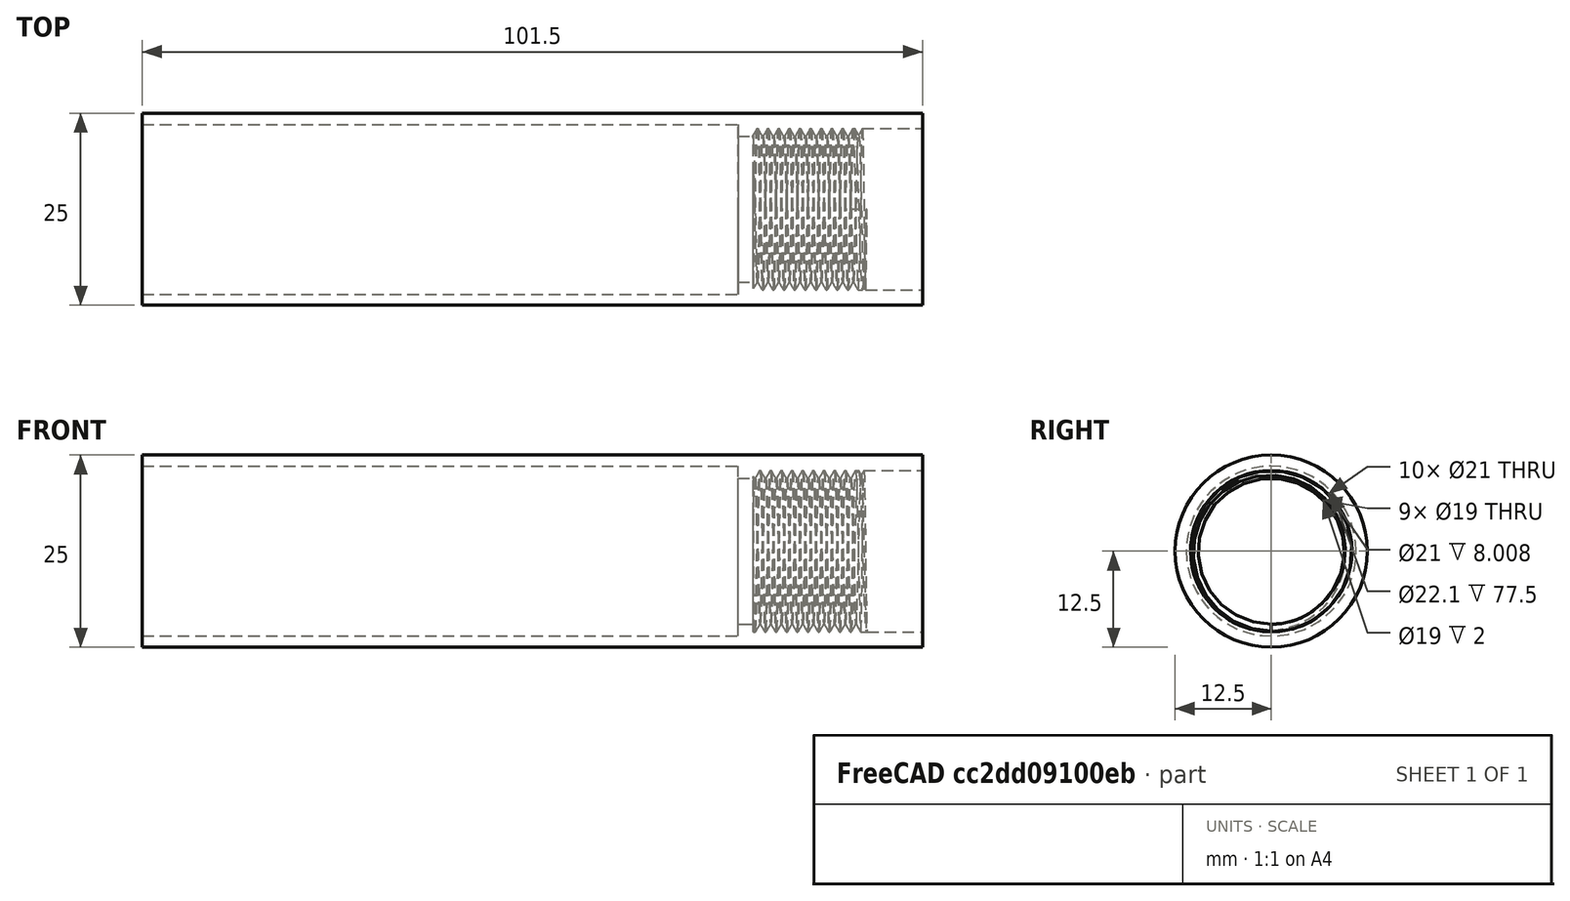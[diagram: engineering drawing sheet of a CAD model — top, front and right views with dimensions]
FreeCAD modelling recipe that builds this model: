
FCSTD DOCUMENT  (FreeCAD 0.17R13541 (Git))
Label: ERG-T-01-BH
License: All rights reserved
LicenseURL: http://en.wikipedia.org/wiki/All_rights_reserved
objects: Drawing::FeatureViewPython×39, Part::Cylinder×6, Part::Cut×5, Drawing::FeatureViewPart×4, Part::MultiFuse×3, Drawing::FeaturePage×2, Sketcher::SketchObject×2, Part::Helix×2, Part::Sweep×2, Part::Feature×1
note: 21 computed .brp shape members not serialized (recipe doc carries the construction recipe); baked Part::Feature solids carry a one-line shape summary decoded from their .brp

FEATURE [Drawing::FeatureViewPython] dim130  # drawing view (typed FeaturePython)
  Rotation = 0
  ViewResult = <g> \n  <line x1="95.000000" y1="103.600000" x2="95.000000" y2="144.306302" style="stroke:rgb(255,0,0);stroke-width:0.10" />\n<line x1="47.000000" y1="102.500000" x2="47.000000" y2="144.306302" style="stroke:rgb(255,0,0);stroke-width:0.10" />\n<line x1="95.000000" y1="143.306302" x2="47.000000" y2="143.306302" style="stroke:rgb(255,0,0);stroke-width:0.10" /> \n  <polygon points="47.000000,143.306302 49.000000,143.806302 49.500000,143.306302 49.000000,142.806302" style="fill:rgb(255,0,0);stroke:rgb(255,0,0);stroke-width:0" /><polygon points="95.000000,143.306302 93.000000,142.806302 92.500000,143.306302 93.000000,143.806302" style="fill:rgb(255,0,0);stroke:rgb(255,0,0);stroke-width:0" /> \n  <text x="71.000000" y="141.306302" font-family="inherit" font-size="3.6" fill="rgb(0,0,0)" text-anchor="middle" transform="rotate(0.000000 71.000000,141.306302)" >24</text> </g>
  Visible = true
  X = 0
  Y = 0
  arrowL1 = 2
  arrowL2 = 0.5
  arrowW = 1
  arrow_scheme = 0
  autoPlaceOffset = 2
  autoPlaceText = true
  click1_x = 59.2162
  click1_y = 143.306
  click2_x = 59.2162
  click2_y = 143.306
  comma_decimal_place = false
  dimension_line_overshoot = 1
  gap_datum_points = 0
  halfDimension_linear = false
  lineColor = rgb(255,0,0)
  strokeWidth = 0.1
  textFormat_linear = %(value)3.3f
  textRenderer_color = rgb(0,0,0)
  textRenderer_family = inherit
  textRenderer_size = 3.6
  unit_custom_scale = 1.7
  unit_scheme = 0
FEATURE [Drawing::FeatureViewPython] dim131  # drawing view (typed FeaturePython)
  Rotation = 0
  ViewResult = <g> \n  <line x1="95.000000" y1="103.600000" x2="95.000000" y2="144.274206" style="stroke:rgb(255,0,0);stroke-width:0.10" />\n<line x1="250.000000" y1="106.500000" x2="250.000000" y2="144.274206" style="stroke:rgb(255,0,0);stroke-width:0.10" />\n<line x1="95.000000" y1="143.274206" x2="250.000000" y2="143.274206" style="stroke:rgb(255,0,0);stroke-width:0.10" /> \n  <polygon points="250.000000,143.274206 248.000000,142.774206 247.500000,143.274206 248.000000,143.774206" style="fill:rgb(255,0,0);stroke:rgb(255,0,0);stroke-width:0" /><polygon points="95.000000,143.274206 97.000000,143.774206 97.500000,143.274206 97.000000,142.774206" style="fill:rgb(255,0,0);stroke:rgb(255,0,0);stroke-width:0" /> \n  <text x="172.500000" y="141.274206" font-family="inherit" font-size="3.6" fill="rgb(0,0,0)" text-anchor="middle" transform="rotate(0.000000 172.500000,141.274206)" >77.5</text> </g>
  Visible = true
  X = 0
  Y = 0
  arrowL1 = 2
  arrowL2 = 0.5
  arrowW = 1
  arrow_scheme = 0
  autoPlaceOffset = 2
  autoPlaceText = true
  click1_x = 247.264
  click1_y = 143.274
  click2_x = 247.264
  click2_y = 143.274
  comma_decimal_place = false
  dimension_line_overshoot = 1
  gap_datum_points = 0
  halfDimension_linear = false
  lineColor = rgb(255,0,0)
  strokeWidth = 0.1
  textFormat_linear = %(value)3.3f
  textRenderer_color = rgb(0,0,0)
  textRenderer_family = inherit
  textRenderer_size = 3.6
  unit_custom_scale = 1.7
  unit_scheme = 0
FEATURE [Drawing::FeatureViewPython] dim132  # drawing view (typed FeaturePython)
  Rotation = 0
  ViewResult = <g> \n  <line x1="95.000000" y1="100.500000" x2="95.000000" y2="91.946246" style="stroke:rgb(255,0,0);stroke-width:0.10" />\n<line x1="91.000000" y1="100.500000" x2="91.000000" y2="91.946246" style="stroke:rgb(255,0,0);stroke-width:0.10" />\n<line x1="95.000000" y1="92.946246" x2="91.000000" y2="92.946246" style="stroke:rgb(255,0,0);stroke-width:0.10" /> \n  <polygon points="91.000000,92.946246 89.000000,92.446246 88.500000,92.946246 89.000000,93.446246" style="fill:rgb(255,0,0);stroke:rgb(255,0,0);stroke-width:0" /><polygon points="95.000000,92.946246 97.000000,93.446246 97.500000,92.946246 97.000000,92.446246" style="fill:rgb(255,0,0);stroke:rgb(255,0,0);stroke-width:0" /> \n  <text x="93.000000" y="90.946246" font-family="inherit" font-size="3.6" fill="rgb(0,0,0)" text-anchor="middle" transform="rotate(0.000000 93.000000,90.946246)" >2</text> </g>
  Visible = true
  X = 0
  Y = 0
  arrowL1 = 2
  arrowL2 = 0.5
  arrowW = 1
  arrow_scheme = 0
  autoPlaceOffset = 2
  autoPlaceText = true
  click1_x = 91.8628
  click1_y = 92.9462
  click2_x = 91.8628
  click2_y = 92.9462
  comma_decimal_place = false
  dimension_line_overshoot = 1
  gap_datum_points = 0
  halfDimension_linear = false
  lineColor = rgb(255,0,0)
  strokeWidth = 0.1
  textFormat_linear = %(value)3.3f
  textRenderer_color = rgb(0,0,0)
  textRenderer_family = inherit
  textRenderer_size = 3.6
  unit_custom_scale = 1.7
  unit_scheme = 0
FEATURE [Drawing::FeatureViewPython] dim133  # drawing view (typed FeaturePython)
  Rotation = 0
  ViewResult = <g> \n  <line x1="62.208000" y1="60.500000" x2="62.208000" y2="72.297691" style="stroke:rgb(255,0,0);stroke-width:0.10" />\n<line x1="91.000000" y1="62.500000" x2="91.000000" y2="72.297691" style="stroke:rgb(255,0,0);stroke-width:0.10" />\n<line x1="62.208000" y1="71.297691" x2="91.000000" y2="71.297691" style="stroke:rgb(255,0,0);stroke-width:0.10" /> \n  <polygon points="91.000000,71.297691 89.000000,70.797691 88.500000,71.297691 89.000000,71.797691" style="fill:rgb(255,0,0);stroke:rgb(255,0,0);stroke-width:0" /><polygon points="62.208000,71.297691 64.208000,71.797691 64.708000,71.297691 64.208000,70.797691" style="fill:rgb(255,0,0);stroke:rgb(255,0,0);stroke-width:0" /> \n  <text x="76.604000" y="69.297691" font-family="inherit" font-size="3.6" fill="rgb(0,0,0)" text-anchor="middle" transform="rotate(0.000000 76.604000,69.297691)" >14.2</text> </g>
  Visible = true
  X = 0
  Y = 0
  arrowL1 = 2
  arrowL2 = 0.5
  arrowW = 1
  arrow_scheme = 0
  autoPlaceOffset = 2
  autoPlaceText = true
  click1_x = 89.6096
  click1_y = 71.2977
  click2_x = 89.6096
  click2_y = 71.2977
  comma_decimal_place = false
  dimension_line_overshoot = 1
  gap_datum_points = 0
  halfDimension_linear = false
  lineColor = rgb(255,0,0)
  strokeWidth = 0.1
  textFormat_linear = 14.2
  textRenderer_color = rgb(0,0,0)
  textRenderer_family = inherit
  textRenderer_size = 3.6
  unit_custom_scale = 1.7
  unit_scheme = 0
FEATURE [Drawing::FeatureViewPython] dim134  # drawing view (typed FeaturePython)
  Rotation = 0
  ViewResult = <g> \n  <line x1="47.000000" y1="60.500000" x2="47.000000" y2="72.294300" style="stroke:rgb(255,0,0);stroke-width:0.10" />\n<line x1="62.208000" y1="60.500000" x2="62.208000" y2="72.294300" style="stroke:rgb(255,0,0);stroke-width:0.10" />\n<line x1="47.000000" y1="71.294300" x2="62.208000" y2="71.294300" style="stroke:rgb(255,0,0);stroke-width:0.10" /> \n  <polygon points="62.208000,71.294300 60.208000,70.794300 59.708000,71.294300 60.208000,71.794300" style="fill:rgb(255,0,0);stroke:rgb(255,0,0);stroke-width:0" /><polygon points="47.000000,71.294300 49.000000,71.794300 49.500000,71.294300 49.000000,70.794300" style="fill:rgb(255,0,0);stroke:rgb(255,0,0);stroke-width:0" /> \n  <text x="54.604000" y="69.294300" font-family="inherit" font-size="3.6" fill="rgb(0,0,0)" text-anchor="middle" transform="rotate(0.000000 54.604000,69.294300)" >7.8</text> </g>
  Visible = true
  X = 0
  Y = 0
  arrowL1 = 2
  arrowL2 = 0.5
  arrowW = 1
  arrow_scheme = 0
  autoPlaceOffset = 2
  autoPlaceText = true
  click1_x = 60.9176
  click1_y = 71.2943
  click2_x = 60.9176
  click2_y = 71.2943
  comma_decimal_place = false
  dimension_line_overshoot = 1
  gap_datum_points = 0
  halfDimension_linear = false
  lineColor = rgb(255,0,0)
  strokeWidth = 0.1
  textFormat_linear = 7.8
  textRenderer_color = rgb(0,0,0)
  textRenderer_family = inherit
  textRenderer_size = 3.6
  unit_custom_scale = 1.7
  unit_scheme = 0
FEATURE [Drawing::FeatureViewPython] dim160  # drawing view (typed FeaturePython)
  Rotation = 0
  ViewResult = <g> \n  <line x1="250.000000" y1="59.400000" x2="266.991260" y2="59.400000" style="stroke:rgb(255,0,0);stroke-width:0.10" />\n<line x1="250.000000" y1="56.500000" x2="266.991260" y2="56.500000" style="stroke:rgb(255,0,0);stroke-width:0.10" />\n<line x1="265.991260" y1="59.400000" x2="265.991260" y2="56.500000" style="stroke:rgb(255,0,0);stroke-width:0.10" /> \n  <polygon points="265.991260,56.500000 266.491260,54.500000 265.991260,54.000000 265.491260,54.500000" style="fill:rgb(255,0,0);stroke:rgb(255,0,0);stroke-width:0" /><polygon points="265.991260,59.400000 265.491260,61.400000 265.991260,61.900000 266.491260,61.400000" style="fill:rgb(255,0,0);stroke:rgb(255,0,0);stroke-width:0" /> \n  <text x="263.991260" y="57.950000" font-family="inherit" font-size="3.6" fill="rgb(0,0,0)" text-anchor="middle" transform="rotate(-90.000000 263.991260,57.950000)" >1.45</text> </g>
  Visible = true
  X = 0
  Y = 0
  arrowL1 = 2
  arrowL2 = 0.5
  arrowW = 1
  arrow_scheme = 0
  autoPlaceOffset = 2
  autoPlaceText = true
  click1_x = 265.991
  click1_y = 61.2489
  click2_x = 265.991
  click2_y = 61.2489
  comma_decimal_place = false
  dimension_line_overshoot = 1
  gap_datum_points = 0
  halfDimension_linear = false
  lineColor = rgb(255,0,0)
  strokeWidth = 0.1
  textFormat_linear = %(value)3.3f
  textRenderer_color = rgb(0,0,0)
  textRenderer_family = inherit
  textRenderer_size = 3.6
  unit_custom_scale = 1.7
  unit_scheme = 0
FEATURE [Drawing::FeatureViewPython] dim161  # drawing view (typed FeaturePython)
  Rotation = 0
  ViewResult = <g> \n  <line x1="250.000000" y1="59.400000" x2="266.857529" y2="59.400000" style="stroke:rgb(255,0,0);stroke-width:0.10" />\n<line x1="250.000000" y1="103.600000" x2="266.857529" y2="103.600000" style="stroke:rgb(255,0,0);stroke-width:0.10" />\n<line x1="265.857529" y1="59.400000" x2="265.857529" y2="103.600000" style="stroke:rgb(255,0,0);stroke-width:0.10" /> \n  <polygon points="265.857529,103.600000 266.357529,101.600000 265.857529,101.100000 265.357529,101.600000" style="fill:rgb(255,0,0);stroke:rgb(255,0,0);stroke-width:0" /><polygon points="265.857529,59.400000 265.357529,61.400000 265.857529,61.900000 266.357529,61.400000" style="fill:rgb(255,0,0);stroke:rgb(255,0,0);stroke-width:0" /> \n  <text x="263.857529" y="81.500000" font-family="inherit" font-size="3.6" fill="rgb(0,0,0)" text-anchor="middle" transform="rotate(-90.000000 263.857529,81.500000)" >22.1</text> </g>
  Visible = true
  X = 0
  Y = 0
  arrowL1 = 2
  arrowL2 = 0.5
  arrowW = 1
  arrow_scheme = 0
  autoPlaceOffset = 2
  autoPlaceText = true
  click1_x = 265.858
  click1_y = 102.973
  click2_x = 265.858
  click2_y = 102.973
  comma_decimal_place = false
  dimension_line_overshoot = 1
  gap_datum_points = 0
  halfDimension_linear = false
  lineColor = rgb(255,0,0)
  strokeWidth = 0.1
  textFormat_linear = %(value)3.3f
  textRenderer_color = rgb(0,0,0)
  textRenderer_family = inherit
  textRenderer_size = 3.6
  unit_custom_scale = 1.7
  unit_scheme = 0
FEATURE [Drawing::FeatureViewPython] dim162  # drawing view (typed FeaturePython)
  Rotation = 0
  ViewResult = <g> \n  <line x1="250.000000" y1="106.500000" x2="266.857529" y2="106.500000" style="stroke:rgb(255,0,0);stroke-width:0.10" />\n<line x1="250.000000" y1="103.600000" x2="266.857529" y2="103.600000" style="stroke:rgb(255,0,0);stroke-width:0.10" />\n<line x1="265.857529" y1="106.500000" x2="265.857529" y2="103.600000" style="stroke:rgb(255,0,0);stroke-width:0.10" /> \n  <polygon points="265.857529,103.600000 266.357529,101.600000 265.857529,101.100000 265.357529,101.600000" style="fill:rgb(255,0,0);stroke:rgb(255,0,0);stroke-width:0" /><polygon points="265.857529,106.500000 265.357529,108.500000 265.857529,109.000000 266.357529,108.500000" style="fill:rgb(255,0,0);stroke:rgb(255,0,0);stroke-width:0" /> \n  <text x="263.857529" y="105.050000" font-family="inherit" font-size="3.6" fill="rgb(0,0,0)" text-anchor="middle" transform="rotate(-90.000000 263.857529,105.050000)" >1.45</text> </g>
  Visible = true
  X = 0
  Y = 0
  arrowL1 = 2
  arrowL2 = 0.5
  arrowW = 1
  arrow_scheme = 0
  autoPlaceOffset = 2
  autoPlaceText = true
  click1_x = 265.858
  click1_y = 105.915
  click2_x = 265.858
  click2_y = 105.915
  comma_decimal_place = false
  dimension_line_overshoot = 1
  gap_datum_points = 0
  halfDimension_linear = false
  lineColor = rgb(255,0,0)
  strokeWidth = 0.1
  textFormat_linear = %(value)3.3f
  textRenderer_color = rgb(0,0,0)
  textRenderer_family = inherit
  textRenderer_size = 3.6
  unit_custom_scale = 1.7
  unit_scheme = 0
FEATURE [Drawing::FeatureViewPython] dim140  # drawing view (typed FeaturePython)
  Rotation = 0
  ViewResult = <g> \n  <line x1="95.000000" y1="62.500000" x2="113.045957" y2="62.500000" style="stroke:rgb(255,0,0);stroke-width:0.10" />\n<line x1="95.000000" y1="100.500000" x2="113.045957" y2="100.500000" style="stroke:rgb(255,0,0);stroke-width:0.10" />\n<line x1="112.045957" y1="62.500000" x2="112.045957" y2="100.500000" style="stroke:rgb(255,0,0);stroke-width:0.10" /> \n  <polygon points="112.045957,100.500000 112.545957,98.500000 112.045957,98.000000 111.545957,98.500000" style="fill:rgb(255,0,0);stroke:rgb(255,0,0);stroke-width:0" /><polygon points="112.045957,62.500000 111.545957,64.500000 112.045957,65.000000 112.545957,64.500000" style="fill:rgb(255,0,0);stroke:rgb(255,0,0);stroke-width:0" /> \n  <text x="110.045957" y="81.500000" font-family="inherit" font-size="3.6" fill="rgb(0,0,0)" text-anchor="middle" transform="rotate(-90.000000 110.045957,81.500000)" >19</text> </g>
  Visible = true
  X = 0
  Y = 0
  arrowL1 = 2
  arrowL2 = 0.5
  arrowW = 1
  arrow_scheme = 0
  autoPlaceOffset = 2
  autoPlaceText = true
  click1_x = 112.046
  click1_y = 100.247
  click2_x = 112.046
  click2_y = 100.247
  comma_decimal_place = false
  dimension_line_overshoot = 1
  gap_datum_points = 0
  halfDimension_linear = false
  lineColor = rgb(255,0,0)
  strokeWidth = 0.1
  textFormat_linear = %(value)3.3f
  textRenderer_color = rgb(0,0,0)
  textRenderer_family = inherit
  textRenderer_size = 3.6
  unit_custom_scale = 1.7
  unit_scheme = 0
FEATURE [Drawing::FeatureViewPython] dim135  # drawing view (typed FeaturePython)
  Rotation = 0
  ViewResult = <g> \n  <line x1="91.000000" y1="100.500000" x2="91.000000" y2="92.012785" style="stroke:rgb(255,0,0);stroke-width:0.10" />\n<line x1="47.000000" y1="102.500000" x2="47.000000" y2="92.012785" style="stroke:rgb(255,0,0);stroke-width:0.10" />\n<line x1="91.000000" y1="93.012785" x2="47.000000" y2="93.012785" style="stroke:rgb(255,0,0);stroke-width:0.10" /> \n  <polygon points="47.000000,93.012785 49.000000,93.512785 49.500000,93.012785 49.000000,92.512785" style="fill:rgb(255,0,0);stroke:rgb(255,0,0);stroke-width:0" /><polygon points="91.000000,93.012785 89.000000,92.512785 88.500000,93.012785 89.000000,93.512785" style="fill:rgb(255,0,0);stroke:rgb(255,0,0);stroke-width:0" /> \n  <text x="69.000000" y="91.012785" font-family="inherit" font-size="3.6" fill="rgb(0,0,0)" text-anchor="middle" transform="rotate(0.000000 69.000000,91.012785)" >22</text> </g>
  Visible = true
  X = 0
  Y = 0
  arrowL1 = 2
  arrowL2 = 0.5
  arrowW = 1
  arrow_scheme = 0
  autoPlaceOffset = 2
  autoPlaceText = true
  click1_x = 47.2505
  click1_y = 93.0128
  click2_x = 47.2505
  click2_y = 93.0128
  comma_decimal_place = false
  dimension_line_overshoot = 1
  gap_datum_points = 0
  halfDimension_linear = false
  lineColor = rgb(255,0,0)
  strokeWidth = 0.1
  textFormat_linear = %(value)3.3f
  textRenderer_color = rgb(0,0,0)
  textRenderer_family = inherit
  textRenderer_size = 3.6
  unit_custom_scale = 1.7
  unit_scheme = 0
FEATURE [Drawing::FeatureViewPython] dim136  # drawing view (typed FeaturePython)
  Rotation = 0
  ViewResult = <g> \n  <line x1="47.000000" y1="60.500000" x2="41.165796" y2="60.500000" style="stroke:rgb(255,0,0);stroke-width:0.10" />\n<line x1="47.000000" y1="56.500000" x2="41.165796" y2="56.500000" style="stroke:rgb(255,0,0);stroke-width:0.10" />\n<line x1="42.165796" y1="60.500000" x2="42.165796" y2="56.500000" style="stroke:rgb(255,0,0);stroke-width:0.10" /> \n  <polygon points="42.165796,56.500000 42.665796,54.500000 42.165796,54.000000 41.665796,54.500000" style="fill:rgb(255,0,0);stroke:rgb(255,0,0);stroke-width:0" /><polygon points="42.165796,60.500000 41.665796,62.500000 42.165796,63.000000 42.665796,62.500000" style="fill:rgb(255,0,0);stroke:rgb(255,0,0);stroke-width:0" /> \n  <text x="40.165796" y="58.500000" font-family="inherit" font-size="3.6" fill="rgb(0,0,0)" text-anchor="middle" transform="rotate(-90.000000 40.165796,58.500000)" >2</text> </g>
  Visible = true
  X = 0
  Y = 0
  arrowL1 = 2
  arrowL2 = 0.5
  arrowW = 1
  arrow_scheme = 0
  autoPlaceOffset = 2
  autoPlaceText = true
  click1_x = 42.1658
  click1_y = 59.7762
  click2_x = 42.1658
  click2_y = 59.7762
  comma_decimal_place = false
  dimension_line_overshoot = 1
  gap_datum_points = 0
  halfDimension_linear = false
  lineColor = rgb(255,0,0)
  strokeWidth = 0.1
  textFormat_linear = %(value)3.3f
  textRenderer_color = rgb(0,0,0)
  textRenderer_family = inherit
  textRenderer_size = 3.6
  unit_custom_scale = 1.7
  unit_scheme = 0
FEATURE [Drawing::FeatureViewPython] dim137  # drawing view (typed FeaturePython)
  Rotation = 0
  ViewResult = <g> \n  <line x1="47.000000" y1="106.500000" x2="41.289813" y2="106.500000" style="stroke:rgb(255,0,0);stroke-width:0.10" />\n<line x1="47.000000" y1="102.500000" x2="41.289813" y2="102.500000" style="stroke:rgb(255,0,0);stroke-width:0.10" />\n<line x1="42.289813" y1="106.500000" x2="42.289813" y2="102.500000" style="stroke:rgb(255,0,0);stroke-width:0.10" /> \n  <polygon points="42.289813,102.500000 42.789813,100.500000 42.289813,100.000000 41.789813,100.500000" style="fill:rgb(255,0,0);stroke:rgb(255,0,0);stroke-width:0" /><polygon points="42.289813,106.500000 41.789813,108.500000 42.289813,109.000000 42.789813,108.500000" style="fill:rgb(255,0,0);stroke:rgb(255,0,0);stroke-width:0" /> \n  <text x="40.289813" y="104.500000" font-family="inherit" font-size="3.6" fill="rgb(0,0,0)" text-anchor="middle" transform="rotate(-90.000000 40.289813,104.500000)" >2</text> </g>
  Visible = true
  X = 0
  Y = 0
  arrowL1 = 2
  arrowL2 = 0.5
  arrowW = 1
  arrow_scheme = 0
  autoPlaceOffset = 2
  autoPlaceText = true
  click1_x = 42.2898
  click1_y = 105.042
  click2_x = 42.2898
  click2_y = 105.042
  comma_decimal_place = false
  dimension_line_overshoot = 1
  gap_datum_points = 0
  halfDimension_linear = false
  lineColor = rgb(255,0,0)
  strokeWidth = 0.1
  textFormat_linear = %(value)3.3f
  textRenderer_color = rgb(0,0,0)
  textRenderer_family = inherit
  textRenderer_size = 3.6
  unit_custom_scale = 1.7
  unit_scheme = 0
FEATURE [Drawing::FeatureViewPython] dim138  # drawing view (typed FeaturePython)
  Rotation = 0
  ViewResult = <g> \n  <line x1="47.000000" y1="60.500000" x2="41.372491" y2="60.500000" style="stroke:rgb(255,0,0);stroke-width:0.10" />\n<line x1="47.000000" y1="102.500000" x2="41.372491" y2="102.500000" style="stroke:rgb(255,0,0);stroke-width:0.10" />\n<line x1="42.372491" y1="60.500000" x2="42.372491" y2="102.500000" style="stroke:rgb(255,0,0);stroke-width:0.10" /> \n  <polygon points="42.372491,102.500000 42.872491,100.500000 42.372491,100.000000 41.872491,100.500000" style="fill:rgb(255,0,0);stroke:rgb(255,0,0);stroke-width:0" /><polygon points="42.372491,60.500000 41.872491,62.500000 42.372491,63.000000 42.872491,62.500000" style="fill:rgb(255,0,0);stroke:rgb(255,0,0);stroke-width:0" /> \n  <text x="40.372491" y="81.500000" font-family="inherit" font-size="3.6" fill="rgb(0,0,0)" text-anchor="middle" transform="rotate(-90.000000 40.372491,81.500000)" >21</text> </g>
  Visible = true
  X = 0
  Y = 0
  arrowL1 = 2
  arrowL2 = 0.5
  arrowW = 1
  arrow_scheme = 0
  autoPlaceOffset = 2
  autoPlaceText = true
  click1_x = 42.3725
  click1_y = 103.244
  click2_x = 42.3725
  click2_y = 103.244
  comma_decimal_place = false
  dimension_line_overshoot = 1
  gap_datum_points = 0
  halfDimension_linear = false
  lineColor = rgb(255,0,0)
  strokeWidth = 0.1
  textFormat_linear = %(value)3.3f
  textRenderer_color = rgb(0,0,0)
  textRenderer_family = inherit
  textRenderer_size = 3.6
  unit_custom_scale = 1.7
  unit_scheme = 0
FEATURE [Drawing::FeatureViewPython] dim139  # drawing view (typed FeaturePython)
  Rotation = 0
  ViewResult = <g> \n  <line x1="250.000000" y1="56.500000" x2="250.000000" y2="34.604582" style="stroke:rgb(255,0,0);stroke-width:0.10" />\n<line x1="47.000000" y1="56.500000" x2="47.000000" y2="34.604582" style="stroke:rgb(255,0,0);stroke-width:0.10" />\n<line x1="250.000000" y1="35.604582" x2="47.000000" y2="35.604582" style="stroke:rgb(255,0,0);stroke-width:0.10" /> \n  <polygon points="47.000000,35.604582 49.000000,36.104582 49.500000,35.604582 49.000000,35.104582" style="fill:rgb(255,0,0);stroke:rgb(255,0,0);stroke-width:0" /><polygon points="250.000000,35.604582 248.000000,35.104582 247.500000,35.604582 248.000000,36.104582" style="fill:rgb(255,0,0);stroke:rgb(255,0,0);stroke-width:0" /> \n  <text x="148.500000" y="33.604582" font-family="inherit" font-size="3.6" fill="rgb(0,0,0)" text-anchor="middle" transform="rotate(0.000000 148.500000,33.604582)" >101.5</text> </g>
  Visible = true
  X = 0
  Y = 0
  arrowL1 = 2
  arrowL2 = 0.5
  arrowW = 1
  arrow_scheme = 0
  autoPlaceOffset = 2
  autoPlaceText = true
  click1_x = 115.03
  click1_y = 35.6046
  click2_x = 115.03
  click2_y = 35.6046
  comma_decimal_place = false
  dimension_line_overshoot = 1
  gap_datum_points = 0
  halfDimension_linear = false
  lineColor = rgb(255,0,0)
  strokeWidth = 0.1
  textFormat_linear = %(value)3.3f
  textRenderer_color = rgb(0,0,0)
  textRenderer_family = inherit
  textRenderer_size = 3.6
  unit_custom_scale = 1.7
  unit_scheme = 0
FEATURE [Drawing::FeatureViewPython] dim141  # drawing view (typed FeaturePython)
  Rotation = 0
  ViewResult = <g> \n  <line x1="47.000000" y1="56.500000" x2="29.002204" y2="56.500000" style="stroke:rgb(255,0,0);stroke-width:0.10" />\n<line x1="47.000000" y1="106.500000" x2="29.002204" y2="106.500000" style="stroke:rgb(255,0,0);stroke-width:0.10" />\n<line x1="30.002204" y1="56.500000" x2="30.002204" y2="106.500000" style="stroke:rgb(255,0,0);stroke-width:0.10" /> \n  <polygon points="30.002204,106.500000 30.502204,104.500000 30.002204,104.000000 29.502204,104.500000" style="fill:rgb(255,0,0);stroke:rgb(255,0,0);stroke-width:0" /><polygon points="30.002204,56.500000 29.502204,58.500000 30.002204,59.000000 30.502204,58.500000" style="fill:rgb(255,0,0);stroke:rgb(255,0,0);stroke-width:0" /> \n  <text x="28.002204" y="81.500000" font-family="inherit" font-size="3.6" fill="rgb(0,0,0)" text-anchor="middle" transform="rotate(-90.000000 28.002204,81.500000)" >25</text> </g>
  Visible = true
  X = 0
  Y = 0
  arrowL1 = 2
  arrowL2 = 0.5
  arrowW = 1
  arrow_scheme = 0
  autoPlaceOffset = 2
  autoPlaceText = true
  click1_x = 30.0022
  click1_y = 105.651
  click2_x = 30.0022
  click2_y = 105.651
  comma_decimal_place = false
  dimension_line_overshoot = 1
  gap_datum_points = 0
  halfDimension_linear = false
  lineColor = rgb(255,0,0)
  strokeWidth = 0.1
  textFormat_linear = %(value)3.3f
  textRenderer_color = rgb(0,0,0)
  textRenderer_family = inherit
  textRenderer_size = 3.6
  unit_custom_scale = 1.7
  unit_scheme = 0
FEATURE [Drawing::FeatureViewPython] dim142  # drawing view (typed FeaturePython)
  Rotation = 0
  ViewResult = <g> \n  <line x1="95.000000" y1="62.500000" x2="112.985098" y2="62.500000" style="stroke:rgb(255,0,0);stroke-width:0.10" />\n<line x1="95.000000" y1="59.400000" x2="112.985098" y2="59.400000" style="stroke:rgb(255,0,0);stroke-width:0.10" />\n<line x1="111.985098" y1="62.500000" x2="111.985098" y2="59.400000" style="stroke:rgb(255,0,0);stroke-width:0.10" /> \n  <polygon points="111.985098,59.400000 112.485098,57.400000 111.985098,56.900000 111.485098,57.400000" style="fill:rgb(255,0,0);stroke:rgb(255,0,0);stroke-width:0" /><polygon points="111.985098,62.500000 111.485098,64.500000 111.985098,65.000000 112.485098,64.500000" style="fill:rgb(255,0,0);stroke:rgb(255,0,0);stroke-width:0" /> \n  <text x="109.985098" y="60.950000" font-family="inherit" font-size="3.6" fill="rgb(0,0,0)" text-anchor="middle" transform="rotate(-90.000000 109.985098,60.950000)" >1.55</text> </g>
  Visible = true
  X = 0
  Y = 0
  arrowL1 = 2
  arrowL2 = 0.5
  arrowW = 1
  arrow_scheme = 0
  autoPlaceOffset = 2
  autoPlaceText = true
  click1_x = 111.985
  click1_y = 67.3609
  click2_x = 111.985
  click2_y = 67.3609
  comma_decimal_place = false
  dimension_line_overshoot = 1
  gap_datum_points = 0
  halfDimension_linear = false
  lineColor = rgb(255,0,0)
  strokeWidth = 0.1
  textFormat_linear = %(value)3.3f
  textRenderer_color = rgb(0,0,0)
  textRenderer_family = inherit
  textRenderer_size = 3.6
  unit_custom_scale = 1.7
  unit_scheme = 0
FEATURE [Drawing::FeatureViewPython] dim143  # drawing view (typed FeaturePython)
  Rotation = 0
  ViewResult = <g> \n  <line x1="95.000000" y1="103.600000" x2="113.079441" y2="103.600000" style="stroke:rgb(255,0,0);stroke-width:0.10" />\n<line x1="95.000000" y1="100.500000" x2="113.079441" y2="100.500000" style="stroke:rgb(255,0,0);stroke-width:0.10" />\n<line x1="112.079441" y1="103.600000" x2="112.079441" y2="100.500000" style="stroke:rgb(255,0,0);stroke-width:0.10" /> \n  <polygon points="112.079441,100.500000 112.579441,98.500000 112.079441,98.000000 111.579441,98.500000" style="fill:rgb(255,0,0);stroke:rgb(255,0,0);stroke-width:0" /><polygon points="112.079441,103.600000 111.579441,105.600000 112.079441,106.100000 112.579441,105.600000" style="fill:rgb(255,0,0);stroke:rgb(255,0,0);stroke-width:0" /> \n  <text x="110.079441" y="102.050000" font-family="inherit" font-size="3.6" fill="rgb(0,0,0)" text-anchor="middle" transform="rotate(-90.000000 110.079441,102.050000)" >1.55</text> </g>
  Visible = true
  X = 0
  Y = 0
  arrowL1 = 2
  arrowL2 = 0.5
  arrowW = 1
  arrow_scheme = 0
  autoPlaceOffset = 2
  autoPlaceText = true
  click1_x = 112.079
  click1_y = 102.928
  click2_x = 112.079
  click2_y = 102.928
  comma_decimal_place = false
  dimension_line_overshoot = 1
  gap_datum_points = 0
  halfDimension_linear = false
  lineColor = rgb(255,0,0)
  strokeWidth = 0.1
  textFormat_linear = %(value)3.3f
  textRenderer_color = rgb(0,0,0)
  textRenderer_family = inherit
  textRenderer_size = 3.6
  unit_custom_scale = 1.7
  unit_scheme = 0
FEATURE [Drawing::FeatureViewPython] dim144  # drawing view (typed FeaturePython)
  Rotation = 0
  ViewResult = <g> \n  <line x1="63.016000" y1="102.500000" x2="56.047841" y2="102.500000" style="stroke:rgb(255,0,0);stroke-width:0.10" />\n<line x1="64.170000" y1="100.500000" x2="56.047841" y2="100.500000" style="stroke:rgb(255,0,0);stroke-width:0.10" />\n<line x1="57.047841" y1="102.500000" x2="57.047841" y2="100.500000" style="stroke:rgb(255,0,0);stroke-width:0.10" /> \n  <polygon points="57.047841,100.500000 57.547841,98.500000 57.047841,98.000000 56.547841,98.500000" style="fill:rgb(255,0,0);stroke:rgb(255,0,0);stroke-width:0" /><polygon points="57.047841,102.500000 56.547841,104.500000 57.047841,105.000000 57.547841,104.500000" style="fill:rgb(255,0,0);stroke:rgb(255,0,0);stroke-width:0" /> \n  <text x="55.047841" y="101.500000" font-family="inherit" font-size="3.6" fill="rgb(0,0,0)" text-anchor="middle" transform="rotate(-90.000000 55.047841,101.500000)" >1</text> </g>
  Visible = true
  X = 0
  Y = 0
  arrowL1 = 2
  arrowL2 = 0.5
  arrowW = 1
  arrow_scheme = 0
  autoPlaceOffset = 2
  autoPlaceText = true
  click1_x = 57.0478
  click1_y = 102.417
  click2_x = 57.0478
  click2_y = 102.417
  comma_decimal_place = false
  dimension_line_overshoot = 1
  gap_datum_points = 0
  halfDimension_linear = false
  lineColor = rgb(255,0,0)
  strokeWidth = 0.1
  textFormat_linear = %(value)3.3f
  textRenderer_color = rgb(0,0,0)
  textRenderer_family = inherit
  textRenderer_size = 3.6
  unit_custom_scale = 1.7
  unit_scheme = 0
FEATURE [Drawing::FeatureViewPython] dim146  # drawing view (typed FeaturePython)
  Rotation = 0
  ViewResult = <g> \n  <line x1="71.330000" y1="102.500000" x2="71.330000" y2="113.737333" style="stroke:rgb(255,0,0);stroke-width:0.10" />\n<line x1="74.100000" y1="102.500000" x2="74.100000" y2="113.737333" style="stroke:rgb(255,0,0);stroke-width:0.10" />\n<line x1="71.330000" y1="112.737333" x2="74.100000" y2="112.737333" style="stroke:rgb(255,0,0);stroke-width:0.10" /> \n  <polygon points="74.100000,112.737333 76.100000,113.237333 76.600000,112.737333 76.100000,112.237333" style="fill:rgb(255,0,0);stroke:rgb(255,0,0);stroke-width:0" /><polygon points="71.330000,112.737333 69.330000,112.237333 68.830000,112.737333 69.330000,113.237333" style="fill:rgb(255,0,0);stroke:rgb(255,0,0);stroke-width:0" /> \n  <text x="72.715000" y="110.737333" font-family="inherit" font-size="3.6" fill="rgb(0,0,0)" text-anchor="middle" transform="rotate(0.000000 72.715000,110.737333)" >1.4</text> </g>
  Visible = true
  X = 0
  Y = 0
  arrowL1 = 2
  arrowL2 = 0.5
  arrowW = 1
  arrow_scheme = 0
  autoPlaceOffset = 2
  autoPlaceText = true
  click1_x = 74.5203
  click1_y = 112.737
  click2_x = 74.5203
  click2_y = 112.737
  comma_decimal_place = false
  dimension_line_overshoot = 1
  gap_datum_points = 0
  halfDimension_linear = false
  lineColor = rgb(255,0,0)
  strokeWidth = 0.1
  textFormat_linear = %(value)3.1f
  textRenderer_color = rgb(0,0,0)
  textRenderer_family = inherit
  textRenderer_size = 3.6
  unit_custom_scale = 1.7
  unit_scheme = 0
FEATURE [Part::Feature] Fusion003_cs003
  shape: bbox 101.5 x 6.566e-05 x 25 mm, 0 faces, 0 solids (baked)
FEATURE [Drawing::FeatureViewPart] Ortho019  label="Ortho_0_009"
  Direction = (0,1,0)
  HiddenWidth = 0.15
  LineWidth = 0.35
  Rotation = -90
  Scale = 2
  ShowHiddenLines = false
  ShowSmoothLines = false
  Source = -> Fusion003_cs003
  Tolerance = 0.05
  ViewResult = <blob: 5370 chars omitted>
  Visible = true
  X = 406
  Y = 81.5
FEATURE [Drawing::FeaturePage] Page008  label="BatteryHolder2-CS"
  EditableTexts = Dr. Zoidberg | 05.02.2019 | x2.0 | unknown | ERG-T-01 | Battery Holder. Cross Section. | 03 | 03
  Group = -> [Ortho019,dim130,dim131,dim132,dim133,dim134,dim135,dim136,dim137,dim138,dim139,dim141,dim142,dim143,dim144,dim146,dim160,dim161,dim162,dim140]
  Template = <path>//share/freecad/Mod/Drawing/Templates/A4_Landscape.svg
FEATURE [Sketcher::SketchObject] Sketch007  label="T006"
  Placement = pos=(157,0,-10.6) rot=(1,0,0;1.5708rad)
  sketch-geometry (3):
    g0: LineSegment StartX=0.00120621 StartY=1.19996 StartZ=0 EndX=-0.691594 EndY=0 EndZ=0
    g1: LineSegment StartX=0.694006 StartY=0 StartZ=0 EndX=0.00120621 EndY=1.19996 EndZ=0
    g2: LineSegment StartX=-0.691594 StartY=0 StartZ=0 EndX=0.694006 EndY=0 EndZ=0
  constraints (8):
    c: PointOnObject(g1,g-1)
    c: Coincident(g1,g0)
    c: Coincident(g2,g0)
    c: Coincident(g2,g1)
    c: Horizontal(g2)
    c: Angle(g2,g0) = 1.0472
    c: Angle(g1,g2) = 1.0472
    c: Distance(g0,g0) = 1.3856
FEATURE [Drawing::FeatureViewPython] dim151  # drawing view (typed FeaturePython)
  Rotation = 0
  ViewResult = <g> \n  <line x1="105.354000" y1="71.000000" x2="105.354000" y2="61.815462" style="stroke:rgb(255,0,0);stroke-width:0.10" />\n<line x1="97.750000" y1="71.000000" x2="97.750000" y2="61.815462" style="stroke:rgb(255,0,0);stroke-width:0.10" />\n<line x1="105.354000" y1="62.815462" x2="97.750000" y2="62.815462" style="stroke:rgb(255,0,0);stroke-width:0.10" /> \n  <polygon points="97.750000,62.815462 99.750000,63.315462 100.250000,62.815462 99.750000,62.315462" style="fill:rgb(255,0,0);stroke:rgb(255,0,0);stroke-width:0" /><polygon points="105.354000,62.815462 103.354000,62.315462 102.854000,62.815462 103.354000,63.315462" style="fill:rgb(255,0,0);stroke:rgb(255,0,0);stroke-width:0" /> \n  <text x="101.552000" y="60.815462" font-family="inherit" font-size="3.6" fill="rgb(0,0,0)" text-anchor="middle" transform="rotate(0.000000 101.552000,60.815462)" >7.8</text> </g>
  Visible = false
  X = 0
  Y = 0
  arrowL1 = 2
  arrowL2 = 0.5
  arrowW = 1
  arrow_scheme = 0
  autoPlaceOffset = 2
  autoPlaceText = true
  click1_x = 101.962
  click1_y = 62.8155
  click2_x = 101.962
  click2_y = 62.8155
  comma_decimal_place = false
  dimension_line_overshoot = 1
  gap_datum_points = 0
  halfDimension_linear = false
  lineColor = rgb(255,0,0)
  strokeWidth = 0.1
  textFormat_linear = 7.8
  textRenderer_color = rgb(0,0,0)
  textRenderer_family = inherit
  textRenderer_size = 3.6
  unit_custom_scale = 1.7
  unit_scheme = 0
FEATURE [Drawing::FeatureViewPython] dim155  # drawing view (typed FeaturePython)
  Rotation = 0
  ViewResult = <g> \n  <line x1="119.750000" y1="92.000000" x2="119.750000" y2="110.680676" style="stroke:rgb(255,0,0);stroke-width:0.10" />\n<line x1="97.750000" y1="92.000000" x2="97.750000" y2="110.680676" style="stroke:rgb(255,0,0);stroke-width:0.10" />\n<line x1="119.750000" y1="109.680676" x2="97.750000" y2="109.680676" style="stroke:rgb(255,0,0);stroke-width:0.10" /> \n  <polygon points="97.750000,109.680676 99.750000,110.180676 100.250000,109.680676 99.750000,109.180676" style="fill:rgb(255,0,0);stroke:rgb(255,0,0);stroke-width:0" /><polygon points="119.750000,109.680676 117.750000,109.180676 117.250000,109.680676 117.750000,110.180676" style="fill:rgb(255,0,0);stroke:rgb(255,0,0);stroke-width:0" /> \n  <text x="108.750000" y="107.680676" font-family="inherit" font-size="3.6" fill="rgb(0,0,0)" text-anchor="middle" transform="rotate(0.000000 108.750000,107.680676)" >22</text> </g>
  Visible = false
  X = 0
  Y = 0
  arrowL1 = 2
  arrowL2 = 0.5
  arrowW = 1
  arrow_scheme = 0
  autoPlaceOffset = 2
  autoPlaceText = true
  click1_x = 103.281
  click1_y = 109.681
  click2_x = 103.281
  click2_y = 109.681
  comma_decimal_place = false
  dimension_line_overshoot = 1
  gap_datum_points = 0
  halfDimension_linear = false
  lineColor = rgb(255,0,0)
  strokeWidth = 0.1
  textFormat_linear = %(value)3.3f
  textRenderer_color = rgb(0,0,0)
  textRenderer_family = inherit
  textRenderer_size = 3.6
  unit_custom_scale = 1.7
  unit_scheme = 0
FEATURE [Drawing::FeatureViewPython] dim152  # drawing view (typed FeaturePython)
  Rotation = 0
  ViewResult = <g> \n  <line x1="199.250000" y1="70.450000" x2="207.587377" y2="70.450000" style="stroke:rgb(255,0,0);stroke-width:0.10" />\n<line x1="199.250000" y1="92.550000" x2="207.587377" y2="92.550000" style="stroke:rgb(255,0,0);stroke-width:0.10" />\n<line x1="206.587377" y1="70.450000" x2="206.587377" y2="92.550000" style="stroke:rgb(255,0,0);stroke-width:0.10" /> \n  <polygon points="206.587377,92.550000 207.087377,90.550000 206.587377,90.050000 206.087377,90.550000" style="fill:rgb(255,0,0);stroke:rgb(255,0,0);stroke-width:0" /><polygon points="206.587377,70.450000 206.087377,72.450000 206.587377,72.950000 207.087377,72.450000" style="fill:rgb(255,0,0);stroke:rgb(255,0,0);stroke-width:0" /> \n  <text x="204.587377" y="81.500000" font-family="inherit" font-size="3.6" fill="rgb(0,0,0)" text-anchor="middle" transform="rotate(-90.000000 204.587377,81.500000)" >22.1</text> </g>
  Visible = false
  X = 0
  Y = 0
  arrowL1 = 2
  arrowL2 = 0.5
  arrowW = 1
  arrow_scheme = 0
  autoPlaceOffset = 2
  autoPlaceText = true
  click1_x = 206.587
  click1_y = 92.439
  click2_x = 206.587
  click2_y = 92.439
  comma_decimal_place = false
  dimension_line_overshoot = 1
  gap_datum_points = 0
  halfDimension_linear = false
  lineColor = rgb(255,0,0)
  strokeWidth = 0.1
  textFormat_linear = %(value)3.3f
  textRenderer_color = rgb(0,0,0)
  textRenderer_family = inherit
  textRenderer_size = 3.6
  unit_custom_scale = 1.7
  unit_scheme = 0
FEATURE [Drawing::FeatureViewPython] dim153  # drawing view (typed FeaturePython)
  Rotation = 0
  ViewResult = <g> \n  <line x1="199.250000" y1="69.000000" x2="207.587377" y2="69.000000" style="stroke:rgb(255,0,0);stroke-width:0.10" />\n<line x1="199.250000" y1="70.450000" x2="207.587377" y2="70.450000" style="stroke:rgb(255,0,0);stroke-width:0.10" />\n<line x1="206.587377" y1="69.000000" x2="206.587377" y2="70.450000" style="stroke:rgb(255,0,0);stroke-width:0.10" /> \n  <polygon points="206.587377,70.450000 206.087377,72.450000 206.587377,72.950000 207.087377,72.450000" style="fill:rgb(255,0,0);stroke:rgb(255,0,0);stroke-width:0" /><polygon points="206.587377,69.000000 207.087377,67.000000 206.587377,66.500000 206.087377,67.000000" style="fill:rgb(255,0,0);stroke:rgb(255,0,0);stroke-width:0" /> \n  <text x="204.587377" y="69.725000" font-family="inherit" font-size="3.6" fill="rgb(0,0,0)" text-anchor="middle" transform="rotate(-90.000000 204.587377,69.725000)" >1.45</text> </g>
  Visible = false
  X = 0
  Y = 0
  arrowL1 = 2
  arrowL2 = 0.5
  arrowW = 1
  arrow_scheme = 0
  autoPlaceOffset = 2
  autoPlaceText = true
  click1_x = 206.587
  click1_y = 72.2013
  click2_x = 206.587
  click2_y = 72.2013
  comma_decimal_place = false
  dimension_line_overshoot = 1
  gap_datum_points = 0
  halfDimension_linear = false
  lineColor = rgb(255,0,0)
  strokeWidth = 0.1
  textFormat_linear = %(value)3.3f
  textRenderer_color = rgb(0,0,0)
  textRenderer_family = inherit
  textRenderer_size = 3.6
  unit_custom_scale = 1.7
  unit_scheme = 0
FEATURE [Drawing::FeatureViewPython] dim154  # drawing view (typed FeaturePython)
  Rotation = 0
  ViewResult = <g> \n  <line x1="199.250000" y1="92.550000" x2="207.606684" y2="92.550000" style="stroke:rgb(255,0,0);stroke-width:0.10" />\n<line x1="199.250000" y1="94.000000" x2="207.606684" y2="94.000000" style="stroke:rgb(255,0,0);stroke-width:0.10" />\n<line x1="206.606684" y1="92.550000" x2="206.606684" y2="94.000000" style="stroke:rgb(255,0,0);stroke-width:0.10" /> \n  <polygon points="206.606684,94.000000 206.106684,96.000000 206.606684,96.500000 207.106684,96.000000" style="fill:rgb(255,0,0);stroke:rgb(255,0,0);stroke-width:0" /><polygon points="206.606684,92.550000 207.106684,90.550000 206.606684,90.050000 206.106684,90.550000" style="fill:rgb(255,0,0);stroke:rgb(255,0,0);stroke-width:0" /> \n  <text x="204.606684" y="93.275000" font-family="inherit" font-size="3.6" fill="rgb(0,0,0)" text-anchor="middle" transform="rotate(-90.000000 204.606684,93.275000)" >1.45</text> </g>
  Visible = false
  X = 0
  Y = 0
  arrowL1 = 2
  arrowL2 = 0.5
  arrowW = 1
  arrow_scheme = 0
  autoPlaceOffset = 2
  autoPlaceText = true
  click1_x = 206.607
  click1_y = 94.4593
  click2_x = 206.607
  click2_y = 94.4593
  comma_decimal_place = false
  dimension_line_overshoot = 1
  gap_datum_points = 0
  halfDimension_linear = false
  lineColor = rgb(255,0,0)
  strokeWidth = 0.1
  textFormat_linear = %(value)3.3f
  textRenderer_color = rgb(0,0,0)
  textRenderer_family = inherit
  textRenderer_size = 3.6
  unit_custom_scale = 1.7
  unit_scheme = 0
FEATURE [Drawing::FeatureViewPython] dim156  # drawing view (typed FeaturePython)
  Rotation = 0
  ViewResult = <g> \n  <line x1="97.750000" y1="71.000000" x2="86.243697" y2="71.000000" style="stroke:rgb(255,0,0);stroke-width:0.10" />\n<line x1="97.750000" y1="92.000000" x2="86.243697" y2="92.000000" style="stroke:rgb(255,0,0);stroke-width:0.10" />\n<line x1="87.243697" y1="71.000000" x2="87.243697" y2="92.000000" style="stroke:rgb(255,0,0);stroke-width:0.10" /> \n  <polygon points="87.243697,92.000000 87.743697,90.000000 87.243697,89.500000 86.743697,90.000000" style="fill:rgb(255,0,0);stroke:rgb(255,0,0);stroke-width:0" /><polygon points="87.243697,71.000000 86.743697,73.000000 87.243697,73.500000 87.743697,73.000000" style="fill:rgb(255,0,0);stroke:rgb(255,0,0);stroke-width:0" /> \n  <text x="85.243697" y="81.500000" font-family="inherit" font-size="3.6" fill="rgb(0,0,0)" text-anchor="middle" transform="rotate(-90.000000 85.243697,81.500000)" >21</text> </g>
  Visible = false
  X = 0
  Y = 0
  arrowL1 = 2
  arrowL2 = 0.5
  arrowW = 1
  arrow_scheme = 0
  autoPlaceOffset = 2
  autoPlaceText = true
  click1_x = 87.2437
  click1_y = 91.4088
  click2_x = 87.2437
  click2_y = 91.4088
  comma_decimal_place = false
  dimension_line_overshoot = 1
  gap_datum_points = 0
  halfDimension_linear = false
  lineColor = rgb(255,0,0)
  strokeWidth = 0.1
  textFormat_linear = %(value)3.3f
  textRenderer_color = rgb(0,0,0)
  textRenderer_family = inherit
  textRenderer_size = 3.6
  unit_custom_scale = 1.7
  unit_scheme = 0
FEATURE [Drawing::FeatureViewPython] dim157  # drawing view (typed FeaturePython)
  Rotation = 0
  ViewResult = <g> \n  <line x1="107.134000" y1="72.007670" x2="93.667960" y2="72.007670" style="stroke:rgb(255,0,0);stroke-width:0.10" />\n<line x1="107.730000" y1="90.992330" x2="93.667960" y2="90.992330" style="stroke:rgb(255,0,0);stroke-width:0.10" />\n<line x1="94.667960" y1="72.007670" x2="94.667960" y2="90.992330" style="stroke:rgb(255,0,0);stroke-width:0.10" /> \n  <polygon points="94.667960,90.992330 95.167960,88.992330 94.667960,88.492330 94.167960,88.992330" style="fill:rgb(255,0,0);stroke:rgb(255,0,0);stroke-width:0" /><polygon points="94.667960,72.007670 94.167960,74.007670 94.667960,74.507670 95.167960,74.007670" style="fill:rgb(255,0,0);stroke:rgb(255,0,0);stroke-width:0" /> \n  <text x="92.667960" y="81.500000" font-family="inherit" font-size="3.6" fill="rgb(0,0,0)" text-anchor="middle" transform="rotate(-90.000000 92.667960,81.500000)" >19</text> </g>
  Visible = false
  X = 0
  Y = 0
  arrowL1 = 2
  arrowL2 = 0.5
  arrowW = 1
  arrow_scheme = 0
  autoPlaceOffset = 2
  autoPlaceText = true
  click1_x = 94.668
  click1_y = 89.9581
  click2_x = 94.668
  click2_y = 89.9581
  comma_decimal_place = false
  dimension_line_overshoot = 1
  gap_datum_points = 0
  halfDimension_linear = false
  lineColor = rgb(255,0,0)
  strokeWidth = 0.1
  textFormat_linear = %(value)3.1f
  textRenderer_color = rgb(0,0,0)
  textRenderer_family = inherit
  textRenderer_size = 3.6
  unit_custom_scale = 1.7
  unit_scheme = 0
FEATURE [Drawing::FeatureViewPython] dia026  # drawing view (typed FeaturePython)
  Rotation = 0
  ViewResult = <g>  <circle cx ="53.875000" cy ="81.500000" r="0.250000" stroke="none" fill="rgb(255,0,0)" /> \n<line x1="35.510421" y1="129.384504" x2="57.634908" y2="71.696272" style="stroke:rgb(255,0,0);stroke-width:0.10" />\n<polygon points="50.115092,91.303728 51.298109,89.615395 51.010308,88.969507 50.364421,89.257308" style="fill:rgb(255,0,0);stroke:rgb(255,0,0);stroke-width:0" />\n<polygon points="57.634908,71.696272 56.451891,73.384605 56.739692,74.030493 57.385579,73.742692" style="fill:rgb(255,0,0);stroke:rgb(255,0,0);stroke-width:0" />\n<line x1="35.510421" y1="129.384504" x2="26.193330" y2="129.384504" style="stroke:rgb(255,0,0);stroke-width:0.10" />\n<text x="30.851876" y="127.384504" font-family="inherit" font-size="3.6" fill="rgb(0,0,0)" text-anchor="middle" transform="rotate(0.000000 30.851876,127.384504)" >Ø21</text> </g>
  Visible = false
  X = 0
  Y = 0
  arrowL1 = 2
  arrowL2 = 0.5
  arrowW = 1
  arrow_scheme = 0
  autoPlaceOffset = 2
  autoPlaceText = true
  centerPointDia = 0.5
  click1_x = 35.5104
  click1_y = 129.385
  click2_x = 26.1933
  click2_y = 130.439
  click3_x = 26.1933
  click3_y = 130.439
  comma_decimal_place = false
  lineColor = rgb(255,0,0)
  strokeWidth = 0.1
  textFormat_circular = Ø%(value)3.3f
  textRenderer_color = rgb(0,0,0)
  textRenderer_family = inherit
  textRenderer_size = 3.6
  unit_custom_scale = 1.7
  unit_scheme = 0
FEATURE [Drawing::FeatureViewPython] dia024  # drawing view (typed FeaturePython)
  Rotation = 0
  ViewResult = <g>  <circle cx ="243.125000" cy ="81.500000" r="0.250000" stroke="none" fill="rgb(255,0,0)" /> \n<line x1="259.438433" y1="97.490009" x2="236.340569" y2="74.850075" style="stroke:rgb(255,0,0);stroke-width:0.10" />\n<polygon points="249.909431,88.149925 248.831125,86.392865 248.124054,86.399945 248.131133,87.107016" style="fill:rgb(255,0,0);stroke:rgb(255,0,0);stroke-width:0" />\n<polygon points="236.340569,74.850075 237.418875,76.607135 238.125946,76.600055 238.118867,75.892984" style="fill:rgb(255,0,0);stroke:rgb(255,0,0);stroke-width:0" />\n<line x1="259.438433" y1="97.490009" x2="280.166762" y2="97.490009" style="stroke:rgb(255,0,0);stroke-width:0.10" />\n<text x="269.802598" y="95.490009" font-family="inherit" font-size="3.6" fill="rgb(0,0,0)" text-anchor="middle" transform="rotate(0.000000 269.802598,95.490009)" >Ø19</text> </g>
  Visible = false
  X = 0
  Y = 0
  arrowL1 = 2
  arrowL2 = 0.5
  arrowW = 1
  arrow_scheme = 0
  autoPlaceOffset = 2
  autoPlaceText = true
  centerPointDia = 0.5
  click1_x = 259.438
  click1_y = 97.49
  click2_x = 280.167
  click2_y = 102.572
  click3_x = 280.167
  click3_y = 102.572
  comma_decimal_place = false
  lineColor = rgb(255,0,0)
  strokeWidth = 0.1
  textFormat_circular = Ø%(value)3.3f
  textRenderer_color = rgb(0,0,0)
  textRenderer_family = inherit
  textRenderer_size = 3.6
  unit_custom_scale = 1.7
  unit_scheme = 0
FEATURE [Drawing::FeatureViewPython] dia025  # drawing view (typed FeaturePython)
  Rotation = 0
  ViewResult = <g>  <circle cx ="53.875000" cy ="81.500000" r="0.250000" stroke="none" fill="rgb(255,0,0)" /> \n<line x1="29.364657" y1="113.661474" x2="61.451785" y2="71.558052" style="stroke:rgb(255,0,0);stroke-width:0.10" />\n<polygon points="46.298215,91.441948 47.908179,90.154308 47.813572,89.453559 47.112823,89.548165" style="fill:rgb(255,0,0);stroke:rgb(255,0,0);stroke-width:0" />\n<polygon points="61.451785,71.558052 59.841821,72.845692 59.936428,73.546441 60.637177,73.451835" style="fill:rgb(255,0,0);stroke:rgb(255,0,0);stroke-width:0" />\n<line x1="29.364657" y1="113.661474" x2="16.201190" y2="113.661474" style="stroke:rgb(255,0,0);stroke-width:0.10" />\n<text x="22.782924" y="111.661474" font-family="inherit" font-size="3.6" fill="rgb(0,0,0)" text-anchor="middle" transform="rotate(0.000000 22.782924,111.661474)" >Ø25</text> </g>
  Visible = false
  X = 0
  Y = 0
  arrowL1 = 2
  arrowL2 = 0.5
  arrowW = 1
  arrow_scheme = 0
  autoPlaceOffset = 2
  autoPlaceText = true
  centerPointDia = 0.5
  click1_x = 29.3647
  click1_y = 113.661
  click2_x = 16.2012
  click2_y = 116.446
  click3_x = 16.2012
  click3_y = 116.446
  comma_decimal_place = false
  lineColor = rgb(255,0,0)
  strokeWidth = 0.1
  textFormat_circular = Ø%(value)3.3f
  textRenderer_color = rgb(0,0,0)
  textRenderer_family = inherit
  textRenderer_size = 3.6
  unit_custom_scale = 1.7
  unit_scheme = 0
FEATURE [Drawing::FeatureViewPython] dim145  # drawing view (typed FeaturePython)
  Rotation = 0
  ViewResult = <g> \n  <line x1="199.250000" y1="69.000000" x2="199.250000" y2="35.952252" style="stroke:rgb(255,0,0);stroke-width:0.10" />\n<line x1="97.750000" y1="69.000000" x2="97.750000" y2="35.952252" style="stroke:rgb(255,0,0);stroke-width:0.10" />\n<line x1="199.250000" y1="36.952252" x2="97.750000" y2="36.952252" style="stroke:rgb(255,0,0);stroke-width:0.10" /> \n  <polygon points="97.750000,36.952252 99.750000,37.452252 100.250000,36.952252 99.750000,36.452252" style="fill:rgb(255,0,0);stroke:rgb(255,0,0);stroke-width:0" /><polygon points="199.250000,36.952252 197.250000,36.452252 196.750000,36.952252 197.250000,37.452252" style="fill:rgb(255,0,0);stroke:rgb(255,0,0);stroke-width:0" /> \n  <text x="148.500000" y="34.952252" font-family="inherit" font-size="3.6" fill="rgb(0,0,0)" text-anchor="middle" transform="rotate(0.000000 148.500000,34.952252)" >101.5</text> </g>
  Visible = false
  X = 0
  Y = 0
  arrowL1 = 2
  arrowL2 = 0.5
  arrowW = 1
  arrow_scheme = 0
  autoPlaceOffset = 2
  autoPlaceText = true
  click1_x = 163.296
  click1_y = 36.9523
  click2_x = 163.296
  click2_y = 36.9523
  comma_decimal_place = false
  dimension_line_overshoot = 1
  gap_datum_points = 0
  halfDimension_linear = false
  lineColor = rgb(255,0,0)
  strokeWidth = 0.1
  textFormat_linear = %(value)3.3f
  textRenderer_color = rgb(0,0,0)
  textRenderer_family = inherit
  textRenderer_size = 3.6
  unit_custom_scale = 1.7
  unit_scheme = 0
FEATURE [Drawing::FeatureViewPython] dim147  # drawing view (typed FeaturePython)
  Rotation = 0
  ViewResult = <g> \n  <line x1="199.250000" y1="70.450000" x2="199.250000" y2="43.831776" style="stroke:rgb(255,0,0);stroke-width:0.10" />\n<line x1="121.750000" y1="70.450000" x2="121.750000" y2="43.831776" style="stroke:rgb(255,0,0);stroke-width:0.10" />\n<line x1="199.250000" y1="44.831776" x2="121.750000" y2="44.831776" style="stroke:rgb(255,0,0);stroke-width:0.10" /> \n  <polygon points="121.750000,44.831776 123.750000,45.331776 124.250000,44.831776 123.750000,44.331776" style="fill:rgb(255,0,0);stroke:rgb(255,0,0);stroke-width:0" /><polygon points="199.250000,44.831776 197.250000,44.331776 196.750000,44.831776 197.250000,45.331776" style="fill:rgb(255,0,0);stroke:rgb(255,0,0);stroke-width:0" /> \n  <text x="160.500000" y="42.831776" font-family="inherit" font-size="3.6" fill="rgb(0,0,0)" text-anchor="middle" transform="rotate(0.000000 160.500000,42.831776)" >77.5</text> </g>
  Visible = false
  X = 0
  Y = 0
  arrowL1 = 2
  arrowL2 = 0.5
  arrowW = 1
  arrow_scheme = 0
  autoPlaceOffset = 2
  autoPlaceText = true
  click1_x = 154.058
  click1_y = 44.8318
  click2_x = 154.058
  click2_y = 44.8318
  comma_decimal_place = false
  dimension_line_overshoot = 1
  gap_datum_points = 0
  halfDimension_linear = false
  lineColor = rgb(255,0,0)
  strokeWidth = 0.1
  textFormat_linear = %(value)3.3f
  textRenderer_color = rgb(0,0,0)
  textRenderer_family = inherit
  textRenderer_size = 3.6
  unit_custom_scale = 1.7
  unit_scheme = 0
FEATURE [Drawing::FeatureViewPython] dim148  # drawing view (typed FeaturePython)
  Rotation = 0
  ViewResult = <g> \n  <line x1="121.750000" y1="70.450000" x2="121.750000" y2="43.855703" style="stroke:rgb(255,0,0);stroke-width:0.10" />\n<line x1="97.750000" y1="71.000000" x2="97.750000" y2="43.855703" style="stroke:rgb(255,0,0);stroke-width:0.10" />\n<line x1="121.750000" y1="44.855703" x2="97.750000" y2="44.855703" style="stroke:rgb(255,0,0);stroke-width:0.10" /> \n  <polygon points="97.750000,44.855703 99.750000,45.355703 100.250000,44.855703 99.750000,44.355703" style="fill:rgb(255,0,0);stroke:rgb(255,0,0);stroke-width:0" /><polygon points="121.750000,44.855703 119.750000,44.355703 119.250000,44.855703 119.750000,45.355703" style="fill:rgb(255,0,0);stroke:rgb(255,0,0);stroke-width:0" /> \n  <text x="109.750000" y="42.855703" font-family="inherit" font-size="3.6" fill="rgb(0,0,0)" text-anchor="middle" transform="rotate(0.000000 109.750000,42.855703)" >24</text> </g>
  Visible = false
  X = 0
  Y = 0
  arrowL1 = 2
  arrowL2 = 0.5
  arrowW = 1
  arrow_scheme = 0
  autoPlaceOffset = 2
  autoPlaceText = true
  click1_x = 103.993
  click1_y = 44.8557
  click2_x = 103.993
  click2_y = 44.8557
  comma_decimal_place = false
  dimension_line_overshoot = 1
  gap_datum_points = 0
  halfDimension_linear = false
  lineColor = rgb(255,0,0)
  strokeWidth = 0.1
  textFormat_linear = %(value)3.3f
  textRenderer_color = rgb(0,0,0)
  textRenderer_family = inherit
  textRenderer_size = 3.6
  unit_custom_scale = 1.7
  unit_scheme = 0
FEATURE [Drawing::FeatureViewPython] dim149  # drawing view (typed FeaturePython)
  Rotation = 0
  ViewResult = <g> \n  <line x1="121.750000" y1="72.000000" x2="121.750000" y2="61.726215" style="stroke:rgb(255,0,0);stroke-width:0.10" />\n<line x1="119.750000" y1="72.000000" x2="119.750000" y2="61.726215" style="stroke:rgb(255,0,0);stroke-width:0.10" />\n<line x1="121.750000" y1="62.726215" x2="119.750000" y2="62.726215" style="stroke:rgb(255,0,0);stroke-width:0.10" /> \n  <polygon points="119.750000,62.726215 117.750000,62.226215 117.250000,62.726215 117.750000,63.226215" style="fill:rgb(255,0,0);stroke:rgb(255,0,0);stroke-width:0" /><polygon points="121.750000,62.726215 123.750000,63.226215 124.250000,62.726215 123.750000,62.226215" style="fill:rgb(255,0,0);stroke:rgb(255,0,0);stroke-width:0" /> \n  <text x="120.750000" y="60.726215" font-family="inherit" font-size="3.6" fill="rgb(0,0,0)" text-anchor="middle" transform="rotate(0.000000 120.750000,60.726215)" >2</text> </g>
  Visible = false
  X = 0
  Y = 0
  arrowL1 = 2
  arrowL2 = 0.5
  arrowW = 1
  arrow_scheme = 0
  autoPlaceOffset = 2
  autoPlaceText = true
  click1_x = 121.146
  click1_y = 62.7262
  click2_x = 121.146
  click2_y = 62.7262
  comma_decimal_place = false
  dimension_line_overshoot = 1
  gap_datum_points = 0
  halfDimension_linear = false
  lineColor = rgb(255,0,0)
  strokeWidth = 0.1
  textFormat_linear = %(value)3.3f
  textRenderer_color = rgb(0,0,0)
  textRenderer_family = inherit
  textRenderer_size = 3.6
  unit_custom_scale = 1.7
  unit_scheme = 0
FEATURE [Drawing::FeatureViewPython] dim150  # drawing view (typed FeaturePython)
  Rotation = 0
  ViewResult = <g> \n  <line x1="119.750000" y1="71.756480" x2="119.750000" y2="61.779797" style="stroke:rgb(255,0,0);stroke-width:0.10" />\n<line x1="105.353000" y1="71.000200" x2="105.353000" y2="61.779797" style="stroke:rgb(255,0,0);stroke-width:0.10" />\n<line x1="119.750000" y1="62.779797" x2="105.353000" y2="62.779797" style="stroke:rgb(255,0,0);stroke-width:0.10" /> \n  <polygon points="105.353000,62.779797 107.353000,63.279797 107.853000,62.779797 107.353000,62.279797" style="fill:rgb(255,0,0);stroke:rgb(255,0,0);stroke-width:0" /><polygon points="119.750000,62.779797 117.750000,62.279797 117.250000,62.779797 117.750000,63.279797" style="fill:rgb(255,0,0);stroke:rgb(255,0,0);stroke-width:0" /> \n  <text x="112.551500" y="60.779797" font-family="inherit" font-size="3.6" fill="rgb(0,0,0)" text-anchor="middle" transform="rotate(0.000000 112.551500,60.779797)" >14.2</text> </g>
  Visible = false
  X = 0
  Y = 0
  arrowL1 = 2
  arrowL2 = 0.5
  arrowW = 1
  arrow_scheme = 0
  autoPlaceOffset = 2
  autoPlaceText = true
  click1_x = 105.939
  click1_y = 62.7798
  click2_x = 105.939
  click2_y = 62.7798
  comma_decimal_place = false
  dimension_line_overshoot = 1
  gap_datum_points = 0
  halfDimension_linear = false
  lineColor = rgb(255,0,0)
  strokeWidth = 0.1
  textFormat_linear = 14.2
  textRenderer_color = rgb(0,0,0)
  textRenderer_family = inherit
  textRenderer_size = 3.6
  unit_custom_scale = 1.7
  unit_scheme = 0
FEATURE [Part::Cylinder] Cylinder004  label="Cylinder002"
  Angle = 360
  AttacherType = Attacher::AttachEngine3D
  Height = 23.5
  Placement = pos=(156,0,0) rot=(0,1,0;1.5708rad)
  Radius = 10.5
FEATURE [Part::Helix] Helix010
  Angle = 35.82
  AttacherType = Attacher::AttachEngine3D
  Height = 1.3856
  LocalCoord = 0
  Pitch = 1.3856
  Placement = pos=(170.856,0,0) rot=(0,1,0;1.5708rad)
  Radius = 9.5
  Style = 1
FEATURE [Part::Cylinder] Cylinder003  label="Cylinder001"
  Angle = 360
  AttacherType = Attacher::AttachEngine3D
  Height = 78
  Placement = pos=(78,0,0) rot=(0,1,0;1.5708rad)
  Radius = 11.05
FEATURE [Sketcher::SketchObject] Sketch016  label="T015"
  Placement = pos=(170.856,0,-10.6) rot=(1,0,0;1.5708rad)
  sketch-geometry (3):
    g0: LineSegment StartX=0.00120621 StartY=1.19996 StartZ=0 EndX=-0.691594 EndY=0 EndZ=0
    g1: LineSegment StartX=0.694006 StartY=0 StartZ=0 EndX=0.00120621 EndY=1.19996 EndZ=0
    g2: LineSegment StartX=-0.691594 StartY=0 StartZ=0 EndX=0.694006 EndY=0 EndZ=0
  constraints (8):
    c: PointOnObject(g1,g-1)
    c: Coincident(g1,g0)
    c: Coincident(g2,g0)
    c: Coincident(g2,g1)
    c: Horizontal(g2)
    c: Angle(g2,g0) = 1.0472
    c: Angle(g1,g2) = 1.0472
    c: Distance(g0,g0) = 1.3856
FEATURE [Part::Cylinder] Cylinder002  label="Cylinder"
  Angle = 360
  AttacherType = Attacher::AttachEngine3D
  Height = 101.5
  Placement = pos=(78,0,0) rot=(0,1,0;1.5708rad)
  Radius = 12.5
FEATURE [Part::Cut] Cut001
  Base = -> Cylinder002
  Tool = -> Cylinder003
FEATURE [Part::Cylinder] Cylinder013  label="Cylinder011"
  Angle = 360
  AttacherType = Attacher::AttachEngine3D
  Height = 2
  Placement = pos=(155.5,0,0) rot=(0,1,0;1.5708rad)
  Radius = 11.05
FEATURE [Part::Helix] Helix003
  Angle = 0
  AttacherType = Attacher::AttachEngine3D
  Height = 13.856
  LocalCoord = 0
  Pitch = 1.3856
  Placement = pos=(157,0,0) rot=(0,1,0;1.5708rad)
  Radius = 9.5
  Style = 1
FEATURE [Part::Sweep] Sweep004
  Frenet = true
  Sections = -> [Sketch007]
  Solid = true
  Spine = -> Helix003
  Transition = 1
FEATURE [Part::Cylinder] Cylinder015  label="Cylinder014"
  Angle = 360
  AttacherType = Attacher::AttachEngine3D
  Height = 25
  Placement = pos=(150,0,0) rot=(0,1,0;1.5708rad)
  Radius = 9.5
FEATURE [Part::Cut] Cut006
  Base = -> Sweep004
  Tool = -> Cylinder015
FEATURE [Part::Cylinder] Cylinder014  label="Cylinder013"
  Angle = 360
  AttacherType = Attacher::AttachEngine3D
  Height = 2
  Placement = pos=(155.5,0,0) rot=(0,1,0;1.5708rad)
  Radius = 9.5
FEATURE [Part::Cut] Cut004
  Base = -> Cylinder013
  Tool = -> Cylinder014
FEATURE [Part::MultiFuse] Fusion001
  Shapes = -> [Cut006,Cut004]
FEATURE [Part::Cut] Cut002  label="BatteryHolder"
  Base = -> Cut001
  Tool = -> Cylinder004
FEATURE [Part::Sweep] Sweep010
  Frenet = true
  Sections = -> [Sketch016]
  Solid = true
  Spine = -> Helix010
  Transition = 1
FEATURE [Part::Cut] Cut007
  Base = -> Sweep010
  Tool = -> Cylinder015
FEATURE [Part::MultiFuse] Fusion002
  Shapes = -> [Cut007,Fusion001]
FEATURE [Part::MultiFuse] Fusion003  label="BatHolderThread"
  Shapes = -> [Fusion002,Cut002]
FEATURE [Drawing::FeatureViewPart] Ortho020  label="Ortho_0_010"
  Direction = (1,0,0)
  HiddenWidth = 0.15
  LineWidth = 0.35
  Rotation = -90
  ShowHiddenLines = false
  ShowSmoothLines = false
  Source = -> Fusion003
  Tolerance = 0.05
  ViewResult = <blob: 3228 chars omitted>
  Visible = false
  X = 53.875
  Y = 81.5
FEATURE [Drawing::FeatureViewPart] Ortho021  label="Ortho_1_005"
  Direction = (0,1,0)
  HiddenWidth = 0.15
  LineWidth = 0.35
  Rotation = -90
  ShowHiddenLines = true
  ShowSmoothLines = false
  Source = -> Fusion003
  Tolerance = 0.05
  ViewResult = <blob: 45235 chars omitted>
  Visible = false
  X = 277.25
  Y = 81.5
FEATURE [Drawing::FeatureViewPart] Ortho022  label="Ortho_2_001"
  Direction = (-1,0,0)
  HiddenWidth = 0.15
  LineWidth = 0.35
  Rotation = 90
  ShowHiddenLines = false
  ShowSmoothLines = false
  Source = -> Fusion003
  Tolerance = 0.05
  ViewResult = <g id="Ortho_2_001"\n   transform="rotate(90,243.125,81.5) translate(243.125,81.5) scale(1,1)"\n  >\n<g   fill="none"\n   stroke="rgb(0, 0, 0)"\n   stroke-linecap="butt"\n   stroke-linejoin="miter"\n   stroke-width="0.350000"\n   transform="scale(1,-1)"\n  >\n<path d="M9.5,-0.0015244 L9.5,-0.00202623 " /><path d="M9.5,-0.00203307 Q9.49992,-0.363305 9.4724,-0.723571 " /><path d="M9.32043,-1.83836 Q9.17143,-2.59322 8.90311,-3.31431 " /><path d="M8.07486,-5.00466 Q7.90197,-5.2836 7.71028,-5.54992 " /><circle cx ="0" cy ="0" r ="12.5" /><circle cx ="0" cy ="0" r ="11.05" /><circle cx ="0" cy ="0" r ="9.5" /><path d="M-9.5,0.000122513 C-9.49995,0.0184956 -9.49989,0.0368686 -9.49984,0.0552417  C-9.49311,1.35202 -9.21629,2.64711 -8.69229,3.8333  C-8.16978,5.02015 -7.40017,6.09791 -6.44717,6.97739  C-4.92881,8.38709 -2.93717,9.27414 -0.873621,9.45975  C0.50771,9.58834 1.91655,9.40855 3.22132,8.93718  C5.25681,8.2097 7.02303,6.76093 8.13456,4.90703  C9.02472,3.43599 9.50238,1.7194 9.5,-4.04121e-14 " /></g>\n</g>
  Visible = false
  X = 243.125
  Y = 81.5
FEATURE [Drawing::FeatureViewPython] dia027  # drawing view (typed FeaturePython)
  Rotation = 0
  ViewResult = <g>  <circle cx ="53.873613" cy ="81.495730" r="0.250000" stroke="none" fill="rgb(255,0,0)" /> \n<line x1="33.487025" y1="52.731467" x2="59.369479" y2="89.250069" style="stroke:rgb(255,0,0);stroke-width:0.10" />\n<polygon points="48.377748,73.741390 49.126299,75.662242 49.823353,75.781053 49.942164,75.084000" style="fill:rgb(255,0,0);stroke:rgb(255,0,0);stroke-width:0" />\n<polygon points="59.369479,89.250069 58.620928,87.329218 57.923874,87.210406 57.805062,87.907460" style="fill:rgb(255,0,0);stroke:rgb(255,0,0);stroke-width:0" />\n<line x1="33.487025" y1="52.731467" x2="16.785901" y2="52.731467" style="stroke:rgb(255,0,0);stroke-width:0.10" />\n<text x="25.136463" y="50.731467" font-family="inherit" font-size="3.6" fill="rgb(0,0,0)" text-anchor="middle" transform="rotate(0.000000 25.136463,50.731467)" >Ø19</text> </g>
  Visible = false
  X = 0
  Y = 0
  arrowL1 = 2
  arrowL2 = 0.5
  arrowW = 1
  arrow_scheme = 0
  autoPlaceOffset = 2
  autoPlaceText = true
  centerPointDia = 0.5
  click1_x = 33.487
  click1_y = 52.7315
  click2_x = 16.7859
  click2_y = 52.6467
  click3_x = 16.7859
  click3_y = 52.6467
  comma_decimal_place = false
  lineColor = rgb(255,0,0)
  strokeWidth = 0.1
  textFormat_circular = Ø%(value)3.1f
  textRenderer_color = rgb(0,0,0)
  textRenderer_family = inherit
  textRenderer_size = 3.6
  unit_custom_scale = 1.7
  unit_scheme = 0
FEATURE [Drawing::FeatureViewPython] dim158  # drawing view (typed FeaturePython)
  Rotation = 0
  ViewResult = <g> \n  <line x1="121.750000" y1="72.000000" x2="129.686027" y2="72.000000" style="stroke:rgb(255,0,0);stroke-width:0.10" />\n<line x1="121.750000" y1="91.000000" x2="129.686027" y2="91.000000" style="stroke:rgb(255,0,0);stroke-width:0.10" />\n<line x1="128.686027" y1="72.000000" x2="128.686027" y2="91.000000" style="stroke:rgb(255,0,0);stroke-width:0.10" /> \n  <polygon points="128.686027,91.000000 129.186027,89.000000 128.686027,88.500000 128.186027,89.000000" style="fill:rgb(255,0,0);stroke:rgb(255,0,0);stroke-width:0" /><polygon points="128.686027,72.000000 128.186027,74.000000 128.686027,74.500000 129.186027,74.000000" style="fill:rgb(255,0,0);stroke:rgb(255,0,0);stroke-width:0" /> \n  <text x="126.686027" y="81.500000" font-family="inherit" font-size="3.6" fill="rgb(0,0,0)" text-anchor="middle" transform="rotate(-90.000000 126.686027,81.500000)" >19</text> </g>
  Visible = false
  X = 0
  Y = 0
  arrowL1 = 2
  arrowL2 = 0.5
  arrowW = 1
  arrow_scheme = 0
  autoPlaceOffset = 2
  autoPlaceText = true
  click1_x = 128.686
  click1_y = 89.9108
  click2_x = 128.686
  click2_y = 89.9108
  comma_decimal_place = false
  dimension_line_overshoot = 1
  gap_datum_points = 0
  halfDimension_linear = false
  lineColor = rgb(255,0,0)
  strokeWidth = 0.1
  textFormat_linear = %(value)3.3f
  textRenderer_color = rgb(0,0,0)
  textRenderer_family = inherit
  textRenderer_size = 3.6
  unit_custom_scale = 1.7
  unit_scheme = 0
FEATURE [Drawing::FeatureViewPython] dim159  # drawing view (typed FeaturePython)
  Rotation = 0
  ViewResult = <g> \n  <line x1="121.750000" y1="70.450000" x2="136.015665" y2="70.450000" style="stroke:rgb(255,0,0);stroke-width:0.10" />\n<line x1="121.750000" y1="92.550000" x2="136.015665" y2="92.550000" style="stroke:rgb(255,0,0);stroke-width:0.10" />\n<line x1="135.015665" y1="70.450000" x2="135.015665" y2="92.550000" style="stroke:rgb(255,0,0);stroke-width:0.10" /> \n  <polygon points="135.015665,92.550000 135.515665,90.550000 135.015665,90.050000 134.515665,90.550000" style="fill:rgb(255,0,0);stroke:rgb(255,0,0);stroke-width:0" /><polygon points="135.015665,70.450000 134.515665,72.450000 135.015665,72.950000 135.515665,72.450000" style="fill:rgb(255,0,0);stroke:rgb(255,0,0);stroke-width:0" /> \n  <text x="133.015665" y="81.500000" font-family="inherit" font-size="3.6" fill="rgb(0,0,0)" text-anchor="middle" transform="rotate(-90.000000 133.015665,81.500000)" >22.1</text> </g>
  Visible = false
  X = 0
  Y = 0
  arrowL1 = 2
  arrowL2 = 0.5
  arrowW = 1
  arrow_scheme = 0
  autoPlaceOffset = 2
  autoPlaceText = true
  click1_x = 135.016
  click1_y = 92.6519
  click2_x = 135.016
  click2_y = 92.6519
  comma_decimal_place = false
  dimension_line_overshoot = 1
  gap_datum_points = 0
  halfDimension_linear = false
  lineColor = rgb(255,0,0)
  strokeWidth = 0.1
  textFormat_linear = %(value)3.3f
  textRenderer_color = rgb(0,0,0)
  textRenderer_family = inherit
  textRenderer_size = 3.6
  unit_custom_scale = 1.7
  unit_scheme = 0
FEATURE [Drawing::FeatureViewPython] dia022  # drawing view (typed FeaturePython)
  Rotation = 0
  ViewResult = <g>  <circle cx ="243.125000" cy ="81.500000" r="0.250000" stroke="none" fill="rgb(255,0,0)" /> \n<line x1="255.744788" y1="112.753780" x2="238.987727" y2="71.253758" style="stroke:rgb(255,0,0);stroke-width:0.10" />\n<polygon points="247.262273,91.746242 246.977076,89.704512 246.326238,89.428088 246.049814,90.078925" style="fill:rgb(255,0,0);stroke:rgb(255,0,0);stroke-width:0" />\n<polygon points="238.987727,71.253758 239.272924,73.295488 239.923762,73.571912 240.200186,72.921075" style="fill:rgb(255,0,0);stroke:rgb(255,0,0);stroke-width:0" />\n<line x1="255.744788" y1="112.753780" x2="268.461380" y2="112.753780" style="stroke:rgb(255,0,0);stroke-width:0.10" />\n<text x="262.103084" y="110.753780" font-family="inherit" font-size="3.6" fill="rgb(0,0,0)" text-anchor="middle" transform="rotate(0.000000 262.103084,110.753780)" >Ø22.1</text> </g>
  Visible = false
  X = 0
  Y = 0
  arrowL1 = 2
  arrowL2 = 0.5
  arrowW = 1
  arrow_scheme = 0
  autoPlaceOffset = 2
  autoPlaceText = true
  centerPointDia = 0.5
  click1_x = 255.745
  click1_y = 112.754
  click2_x = 268.461
  click2_y = 113.46
  click3_x = 268.461
  click3_y = 113.46
  comma_decimal_place = false
  lineColor = rgb(255,0,0)
  strokeWidth = 0.1
  textFormat_circular = Ø%(value)3.3f
  textRenderer_color = rgb(0,0,0)
  textRenderer_family = inherit
  textRenderer_size = 3.6
  unit_custom_scale = 1.7
  unit_scheme = 0
FEATURE [Drawing::FeatureViewPython] dia023  # drawing view (typed FeaturePython)
  Rotation = 0
  ViewResult = <g>  <circle cx ="243.125000" cy ="81.500000" r="0.250000" stroke="none" fill="rgb(255,0,0)" /> \n<line x1="260.195596" y1="61.816765" x2="234.935138" y2="90.943313" style="stroke:rgb(255,0,0);stroke-width:0.10" />\n<polygon points="251.314862,72.056687 249.626752,73.240023 249.676890,73.945350 250.382217,73.895212" style="fill:rgb(255,0,0);stroke:rgb(255,0,0);stroke-width:0" />\n<polygon points="234.935138,90.943313 236.623248,89.759977 236.573110,89.054650 235.867783,89.104788" style="fill:rgb(255,0,0);stroke:rgb(255,0,0);stroke-width:0" />\n<line x1="260.195596" y1="61.816765" x2="271.287289" y2="61.816765" style="stroke:rgb(255,0,0);stroke-width:0.10" />\n<text x="265.741443" y="59.816765" font-family="inherit" font-size="3.6" fill="rgb(0,0,0)" text-anchor="middle" transform="rotate(0.000000 265.741443,59.816765)" >Ø25</text> </g>
  Visible = false
  X = 0
  Y = 0
  arrowL1 = 2
  arrowL2 = 0.5
  arrowW = 1
  arrow_scheme = 0
  autoPlaceOffset = 2
  autoPlaceText = true
  centerPointDia = 0.5
  click1_x = 260.196
  click1_y = 61.8168
  click2_x = 271.287
  click2_y = 61.8168
  click3_x = 271.287
  click3_y = 61.8168
  comma_decimal_place = false
  lineColor = rgb(255,0,0)
  strokeWidth = 0.1
  textFormat_circular = Ø%(value)3.3f
  textRenderer_color = rgb(0,0,0)
  textRenderer_family = inherit
  textRenderer_size = 3.6
  unit_custom_scale = 1.7
  unit_scheme = 0
FEATURE [Drawing::FeaturePage] Page009  label="BatteryHolder2-SV"
  EditableTexts = Dr. Zoidberg | 05.02.2019 | x1.0 | unknown | ERG-T-01 | Battery Holder. Side view. | 04 | 04
  Group = -> [Ortho022,Ortho021,Ortho020,dia024,dia025,dim145,dim147,dim148,dim149,dim150,dim151,dim155,dim152,dim153,dim154,dim156,dim157,dia026,dia027,dim158,dim159,dia022,dia023]
  Template = <path>//share/freecad/Mod/Drawing/Templates/A4_Landscape.svg
note: 2 file-system paths scrubbed to <path> (originals preserved in the JSON sidecar)
